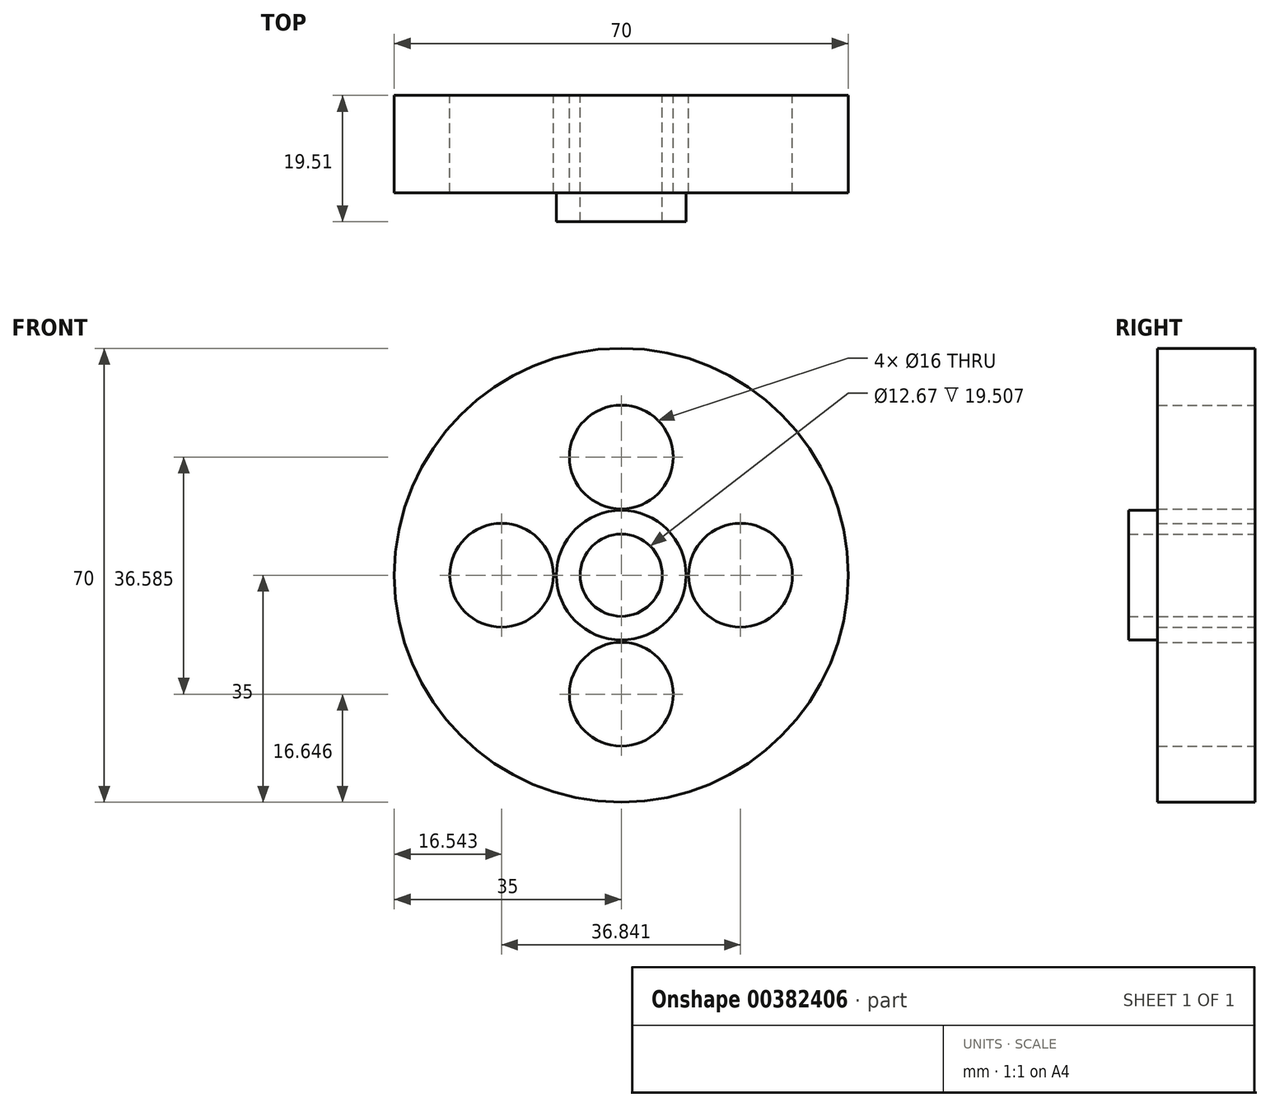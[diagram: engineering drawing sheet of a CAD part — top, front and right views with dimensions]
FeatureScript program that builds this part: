
annotation { "Feature Type Name" : "Feature", "Feature Type Description" : "" }
export const myFeature = defineFeature(function(context is Context, id is Id, definition is map)
    precondition{}
    {
        {
            var Q0;
            Q0=qCreatedBy(makeId("Front.planeOp"),FACE);
            var sketch = newSketch(context, id + "F0", { "sketchPlane" : qUnion([Q0])});
            skCircle(sketch, "E0", {"center": v(0, 0) * mm, "radius": 30 * mm});
            skCircle(sketch, "E1", {"center": v(0, 0) * mm, "radius": 35 * mm});
            skCircle(sketch, "E2", {"center": v(0, 0) * mm, "radius": 10 * mm});
            skCircle(sketch, "E3", {"center": v(0, 0) * mm, "radius": 6.34 * mm});
            skCircle(sketch, "E4", {"center": v(0, 18.23) * mm, "radius": 8 * mm});
            skCircle(sketch, "E5", {"center": v(-18.46, 0) * mm, "radius": 8 * mm});
            skCircle(sketch, "E6", {"center": v(18.38, 0) * mm, "radius": 8 * mm});
            skCircle(sketch, "E7", {"center": v(0, -18.35) * mm, "radius": 8 * mm});
            skSolve(sketch);
        }
        {
            var Q0;
            Q0=makeQuery(id+"F0.imprint","IMPRINT",FACE,{"disambiguationData":[TD([[makeQuery(id+"F0.imprint","IMPRINT",EDGE,{"derivedFrom":sQuery(id+"F0.wireOp",EDGE,"E0")}),-1.0]])]});
            var Q1;
            Q1=makeQuery(id+"F0.imprint","IMPRINT",FACE,{"disambiguationData":[TD([[makeQuery(id+"F0.imprint","IMPRINT",EDGE,{"derivedFrom":sQuery(id+"F0.wireOp",EDGE,"E0")}),1.0]])]});
            extrude(context, id + "F1", {"entities" : qUnion([Q0, Q1]), "depth" : 15 * mm});
        }
        {
            var Q0;
            Q0=makeQuery(id+"F0.imprint","IMPRINT",FACE,{"disambiguationData":[TD([[makeQuery(id+"F0.imprint","IMPRINT",EDGE,{"derivedFrom":sQuery(id+"F0.wireOp",EDGE,"E2")}),1.0]])]});
            extrude(context, id + "F2", {"entities" : qUnion([Q0]), "operationType" : NewBodyOperationType.ADD, "depth" : 19.5 * mm});
        }
    });
